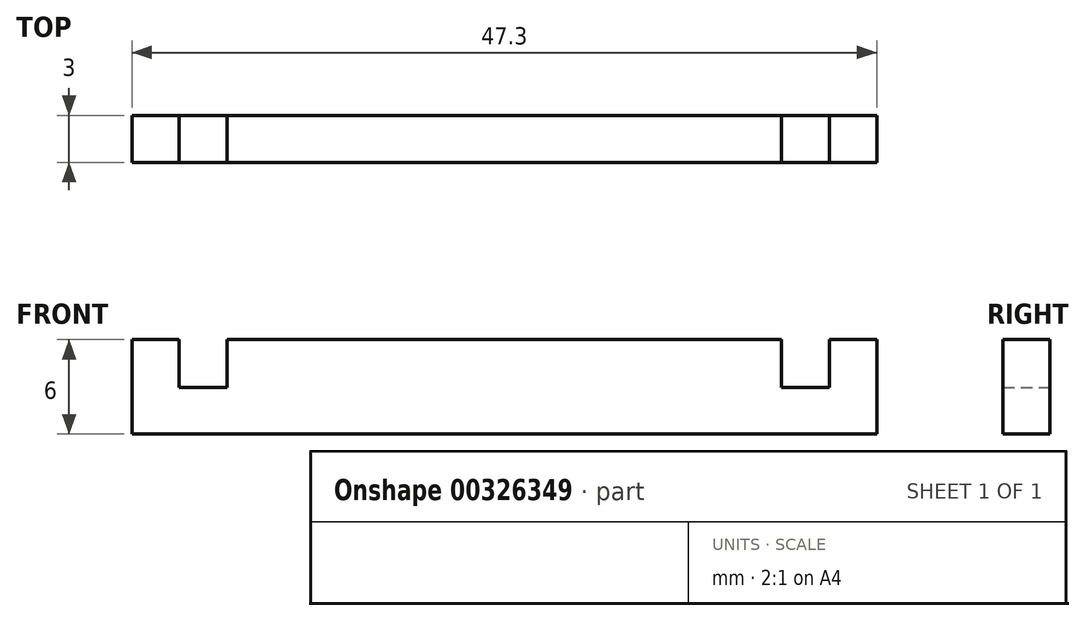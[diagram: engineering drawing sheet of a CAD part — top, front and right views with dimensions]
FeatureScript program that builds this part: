
annotation { "Feature Type Name" : "Feature", "Feature Type Description" : "" }
export const myFeature = defineFeature(function(context is Context, id is Id, definition is map)
    precondition{}
    {
        {
            var Q0;
            Q0=qCreatedBy(makeId("Front.planeOp"),FACE);
            var sketch = newSketch(context, id + "F0", { "sketchPlane" : qUnion([Q0])});
            skLineSegment(sketch, "E0", {"start": v(-25.15, 0) * mm, "end": v(-25.15, 6) * mm});
            skLineSegment(sketch, "E1", {"start": v(-25.15, 6) * mm, "end": v(-22.15, 6) * mm});
            skLineSegment(sketch, "E2", {"start": v(22.15, 6) * mm, "end": v(22.15, 0) * mm});
            skPoint(sketch, "E3", {"position": v(-22.15, 2.98) * mm});
            skPoint(sketch, "E4", {"position": v(-19.11, 2.98) * mm});
            skPoint(sketch, "E5", {"position": v(19.15, 2.98) * mm});
            skPoint(sketch, "E6", {"position": v(16.1, 2.98) * mm});
            skLineSegment(sketch, "E7", {"start": v(-19.11, 2.98) * mm, "end": v(-22.15, 2.98) * mm});
            skLineSegment(sketch, "E8", {"start": v(19.15, 2.98) * mm, "end": v(16.1, 2.98) * mm});
            skLineSegment(sketch, "E9", {"start": v(-25.15, 0) * mm, "end": v(22.15, 0) * mm});
            skLineSegment(sketch, "E10", {"start": v(19.15, 2.98) * mm, "end": v(19.15, 6) * mm});
            skLineSegment(sketch, "E11", {"start": v(16.1, 2.98) * mm, "end": v(16.1, 6) * mm});
            skLineSegment(sketch, "E12", {"start": v(-22.15, 2.98) * mm, "end": v(-22.15, 6) * mm});
            skLineSegment(sketch, "E13", {"start": v(-19.11, 2.98) * mm, "end": v(-19.11, 6) * mm});
            skLineSegment(sketch, "E14.trimOffspring", {"start": v(-19.11, 6) * mm, "end": v(16.1, 6) * mm});
            skLineSegment(sketch, "E15.trimOffspring", {"start": v(19.15, 6) * mm, "end": v(22.15, 6) * mm});
            skSolve(sketch);
        }
        {
            var Q0;
            Q0=makeQuery(id+"F0.imprint","IMPRINT",FACE,{"disambiguationData":[TD([[makeQuery(id+"F0.imprint","IMPRINT",EDGE,{"derivedFrom":sQuery(id+"F0.wireOp",EDGE,"E0")}),-1.0]])]});
            extrude(context, id + "F1", {"entities" : qUnion([Q0]), "depth" : 3 * mm});
        }
    });
